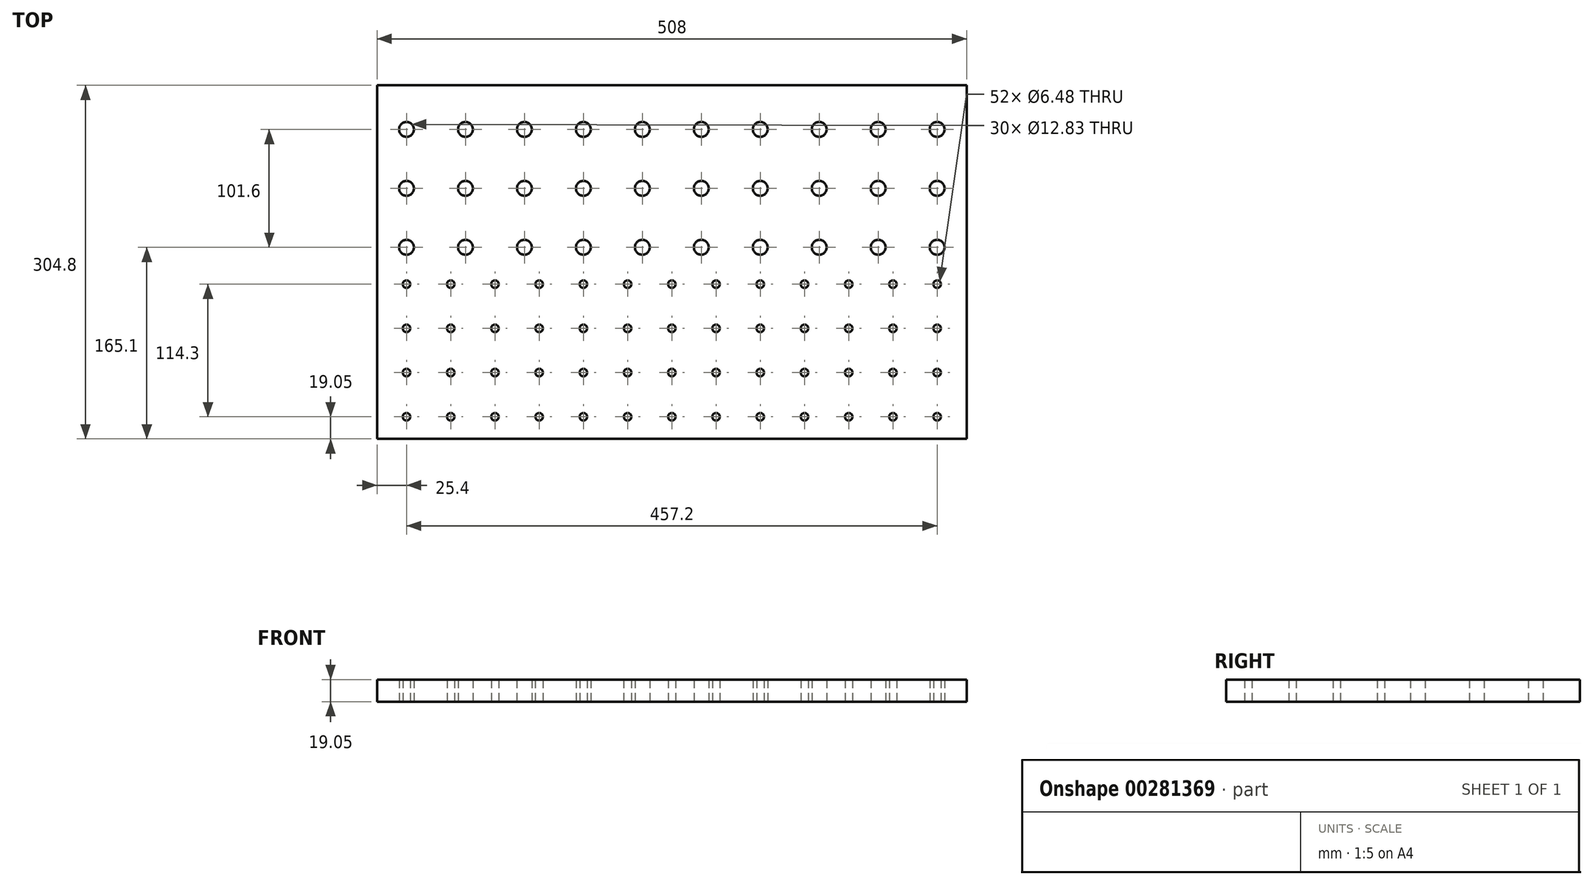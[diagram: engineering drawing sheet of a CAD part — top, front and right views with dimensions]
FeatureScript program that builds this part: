
annotation { "Feature Type Name" : "Feature", "Feature Type Description" : "" }
export const myFeature = defineFeature(function(context is Context, id is Id, definition is map)
    precondition{}
    {
        {
            var Q0;
            Q0=qCreatedBy(makeId("Top.planeOp"),FACE);
            var sketch = newSketch(context, id + "F0", { "sketchPlane" : qUnion([Q0])});
            skLineSegment(sketch, "E0.bottom", {"start": v(254, 152.4) * mm, "end": v(-254, 152.4) * mm});
            skLineSegment(sketch, "E0.top", {"start": v(254, -152.4) * mm, "end": v(-254, -152.4) * mm});
            skLineSegment(sketch, "E0.left", {"start": v(254, 152.4) * mm, "end": v(254, -152.4) * mm});
            skLineSegment(sketch, "E0.right", {"start": v(-254, 152.4) * mm, "end": v(-254, -152.4) * mm});
            skPoint(sketch, "E0.middle", {"position": v(0, 0) * mm});
            skCircle(sketch, "E1", {"center": v(-228.6, 114.3) * mm, "radius": 6.41 * mm});
            skCircle(sketch, "E2.0.1.0", {"center": v(-228.6, 63.5) * mm, "radius": 6.41 * mm});
            skCircle(sketch, "E2.0.2.0", {"center": v(-228.6, 12.7) * mm, "radius": 6.41 * mm});
            skCircle(sketch, "E2.1.0.0", {"center": v(-177.8, 114.3) * mm, "radius": 6.41 * mm});
            skCircle(sketch, "E2.1.1.0", {"center": v(-177.8, 63.5) * mm, "radius": 6.41 * mm});
            skCircle(sketch, "E2.1.2.0", {"center": v(-177.8, 12.7) * mm, "radius": 6.41 * mm});
            skCircle(sketch, "E2.2.0.0", {"center": v(-127, 114.3) * mm, "radius": 6.41 * mm});
            skCircle(sketch, "E2.2.1.0", {"center": v(-127, 63.5) * mm, "radius": 6.41 * mm});
            skCircle(sketch, "E2.2.2.0", {"center": v(-127, 12.7) * mm, "radius": 6.41 * mm});
            skCircle(sketch, "E2.3.0.0", {"center": v(-76.2, 114.3) * mm, "radius": 6.41 * mm});
            skCircle(sketch, "E2.3.1.0", {"center": v(-76.2, 63.5) * mm, "radius": 6.41 * mm});
            skCircle(sketch, "E2.3.2.0", {"center": v(-76.2, 12.7) * mm, "radius": 6.41 * mm});
            skCircle(sketch, "E2.4.0.0", {"center": v(-25.4, 114.3) * mm, "radius": 6.41 * mm});
            skCircle(sketch, "E2.4.1.0", {"center": v(-25.4, 63.5) * mm, "radius": 6.41 * mm});
            skCircle(sketch, "E2.4.2.0", {"center": v(-25.4, 12.7) * mm, "radius": 6.41 * mm});
            skCircle(sketch, "E2.5.0.0", {"center": v(25.4, 114.3) * mm, "radius": 6.41 * mm});
            skCircle(sketch, "E2.5.1.0", {"center": v(25.4, 63.5) * mm, "radius": 6.41 * mm});
            skCircle(sketch, "E2.5.2.0", {"center": v(25.4, 12.7) * mm, "radius": 6.41 * mm});
            skCircle(sketch, "E2.6.0.0", {"center": v(76.2, 114.3) * mm, "radius": 6.41 * mm});
            skCircle(sketch, "E2.6.1.0", {"center": v(76.2, 63.5) * mm, "radius": 6.41 * mm});
            skCircle(sketch, "E2.6.2.0", {"center": v(76.2, 12.7) * mm, "radius": 6.41 * mm});
            skCircle(sketch, "E2.7.0.0", {"center": v(127, 114.3) * mm, "radius": 6.41 * mm});
            skCircle(sketch, "E2.7.1.0", {"center": v(127, 63.5) * mm, "radius": 6.41 * mm});
            skCircle(sketch, "E2.7.2.0", {"center": v(127, 12.7) * mm, "radius": 6.41 * mm});
            skCircle(sketch, "E2.8.0.0", {"center": v(177.8, 114.3) * mm, "radius": 6.41 * mm});
            skCircle(sketch, "E2.8.1.0", {"center": v(177.8, 63.5) * mm, "radius": 6.41 * mm});
            skCircle(sketch, "E2.8.2.0", {"center": v(177.8, 12.7) * mm, "radius": 6.41 * mm});
            skCircle(sketch, "E2.9.0.0", {"center": v(228.6, 114.3) * mm, "radius": 6.41 * mm});
            skCircle(sketch, "E2.9.1.0", {"center": v(228.6, 63.5) * mm, "radius": 6.41 * mm});
            skCircle(sketch, "E2.9.2.0", {"center": v(228.6, 12.7) * mm, "radius": 6.41 * mm});
            skLineSegment(sketch, "E2.direction1", {"start": v(-228.6, 114.3) * mm, "end": v(-177.8, 114.3) * mm, "construction": true});
            skLineSegment(sketch, "E2.direction2", {"start": v(-228.6, 114.3) * mm, "end": v(-228.6, 63.5) * mm, "construction": true});
            skCircle(sketch, "E3", {"center": v(-228.6, -133.35) * mm, "radius": 3.24 * mm});
            skCircle(sketch, "E4.0.1.0", {"center": v(-228.6, -95.25) * mm, "radius": 3.24 * mm});
            skCircle(sketch, "E4.0.2.0", {"center": v(-228.6, -57.15) * mm, "radius": 3.24 * mm});
            skCircle(sketch, "E4.0.3.0", {"center": v(-228.6, -19.05) * mm, "radius": 3.24 * mm});
            skCircle(sketch, "E4.1.0.0", {"center": v(-190.5, -133.35) * mm, "radius": 3.24 * mm});
            skCircle(sketch, "E4.1.1.0", {"center": v(-190.5, -95.25) * mm, "radius": 3.24 * mm});
            skCircle(sketch, "E4.1.2.0", {"center": v(-190.5, -57.15) * mm, "radius": 3.24 * mm});
            skCircle(sketch, "E4.1.3.0", {"center": v(-190.5, -19.05) * mm, "radius": 3.24 * mm});
            skCircle(sketch, "E4.2.0.0", {"center": v(-152.4, -133.35) * mm, "radius": 3.24 * mm});
            skCircle(sketch, "E4.2.1.0", {"center": v(-152.4, -95.25) * mm, "radius": 3.24 * mm});
            skCircle(sketch, "E4.2.2.0", {"center": v(-152.4, -57.15) * mm, "radius": 3.24 * mm});
            skCircle(sketch, "E4.2.3.0", {"center": v(-152.4, -19.05) * mm, "radius": 3.24 * mm});
            skCircle(sketch, "E4.3.0.0", {"center": v(-114.3, -133.35) * mm, "radius": 3.24 * mm});
            skCircle(sketch, "E4.3.1.0", {"center": v(-114.3, -95.25) * mm, "radius": 3.24 * mm});
            skCircle(sketch, "E4.3.2.0", {"center": v(-114.3, -57.15) * mm, "radius": 3.24 * mm});
            skCircle(sketch, "E4.3.3.0", {"center": v(-114.3, -19.05) * mm, "radius": 3.24 * mm});
            skCircle(sketch, "E4.4.0.0", {"center": v(-76.2, -133.35) * mm, "radius": 3.24 * mm});
            skCircle(sketch, "E4.4.1.0", {"center": v(-76.2, -95.25) * mm, "radius": 3.24 * mm});
            skCircle(sketch, "E4.4.2.0", {"center": v(-76.2, -57.15) * mm, "radius": 3.24 * mm});
            skCircle(sketch, "E4.4.3.0", {"center": v(-76.2, -19.05) * mm, "radius": 3.24 * mm});
            skCircle(sketch, "E4.5.0.0", {"center": v(-38.1, -133.35) * mm, "radius": 3.24 * mm});
            skCircle(sketch, "E4.5.1.0", {"center": v(-38.1, -95.25) * mm, "radius": 3.24 * mm});
            skCircle(sketch, "E4.5.2.0", {"center": v(-38.1, -57.15) * mm, "radius": 3.24 * mm});
            skCircle(sketch, "E4.5.3.0", {"center": v(-38.1, -19.05) * mm, "radius": 3.24 * mm});
            skCircle(sketch, "E4.6.0.0", {"center": v(0, -133.35) * mm, "radius": 3.24 * mm});
            skCircle(sketch, "E4.6.1.0", {"center": v(0, -95.25) * mm, "radius": 3.24 * mm});
            skCircle(sketch, "E4.6.2.0", {"center": v(0, -57.15) * mm, "radius": 3.24 * mm});
            skCircle(sketch, "E4.6.3.0", {"center": v(0, -19.05) * mm, "radius": 3.24 * mm});
            skCircle(sketch, "E4.7.0.0", {"center": v(38.1, -133.35) * mm, "radius": 3.24 * mm});
            skCircle(sketch, "E4.7.1.0", {"center": v(38.1, -95.25) * mm, "radius": 3.24 * mm});
            skCircle(sketch, "E4.7.2.0", {"center": v(38.1, -57.15) * mm, "radius": 3.24 * mm});
            skCircle(sketch, "E4.7.3.0", {"center": v(38.1, -19.05) * mm, "radius": 3.24 * mm});
            skCircle(sketch, "E4.8.0.0", {"center": v(76.2, -133.35) * mm, "radius": 3.24 * mm});
            skCircle(sketch, "E4.8.1.0", {"center": v(76.2, -95.25) * mm, "radius": 3.24 * mm});
            skCircle(sketch, "E4.8.2.0", {"center": v(76.2, -57.15) * mm, "radius": 3.24 * mm});
            skCircle(sketch, "E4.8.3.0", {"center": v(76.2, -19.05) * mm, "radius": 3.24 * mm});
            skCircle(sketch, "E4.9.0.0", {"center": v(114.3, -133.35) * mm, "radius": 3.24 * mm});
            skCircle(sketch, "E4.9.1.0", {"center": v(114.3, -95.25) * mm, "radius": 3.24 * mm});
            skCircle(sketch, "E4.9.2.0", {"center": v(114.3, -57.15) * mm, "radius": 3.24 * mm});
            skCircle(sketch, "E4.9.3.0", {"center": v(114.3, -19.05) * mm, "radius": 3.24 * mm});
            skCircle(sketch, "E4.10.0.0", {"center": v(152.4, -133.35) * mm, "radius": 3.24 * mm});
            skCircle(sketch, "E4.10.1.0", {"center": v(152.4, -95.25) * mm, "radius": 3.24 * mm});
            skCircle(sketch, "E4.10.2.0", {"center": v(152.4, -57.15) * mm, "radius": 3.24 * mm});
            skCircle(sketch, "E4.10.3.0", {"center": v(152.4, -19.05) * mm, "radius": 3.24 * mm});
            skCircle(sketch, "E4.11.0.0", {"center": v(190.5, -133.35) * mm, "radius": 3.24 * mm});
            skCircle(sketch, "E4.11.1.0", {"center": v(190.5, -95.25) * mm, "radius": 3.24 * mm});
            skCircle(sketch, "E4.11.2.0", {"center": v(190.5, -57.15) * mm, "radius": 3.24 * mm});
            skCircle(sketch, "E4.11.3.0", {"center": v(190.5, -19.05) * mm, "radius": 3.24 * mm});
            skCircle(sketch, "E4.12.0.0", {"center": v(228.6, -133.35) * mm, "radius": 3.24 * mm});
            skCircle(sketch, "E4.12.1.0", {"center": v(228.6, -95.25) * mm, "radius": 3.24 * mm});
            skCircle(sketch, "E4.12.2.0", {"center": v(228.6, -57.15) * mm, "radius": 3.24 * mm});
            skCircle(sketch, "E4.12.3.0", {"center": v(228.6, -19.05) * mm, "radius": 3.24 * mm});
            skLineSegment(sketch, "E4.direction1", {"start": v(-228.6, -133.35) * mm, "end": v(-190.5, -133.35) * mm, "construction": true});
            skLineSegment(sketch, "E4.direction2", {"start": v(-228.6, -133.35) * mm, "end": v(-228.6, -95.25) * mm, "construction": true});
            skSolve(sketch);
        }
        {
            var Q0;
            Q0 = qSketchRegion(id + "F0", true);
            extrude(context, id + "F1", {"entities" : qUnion([Q0]), "depth" : 19.05 * mm});
        }
    });
